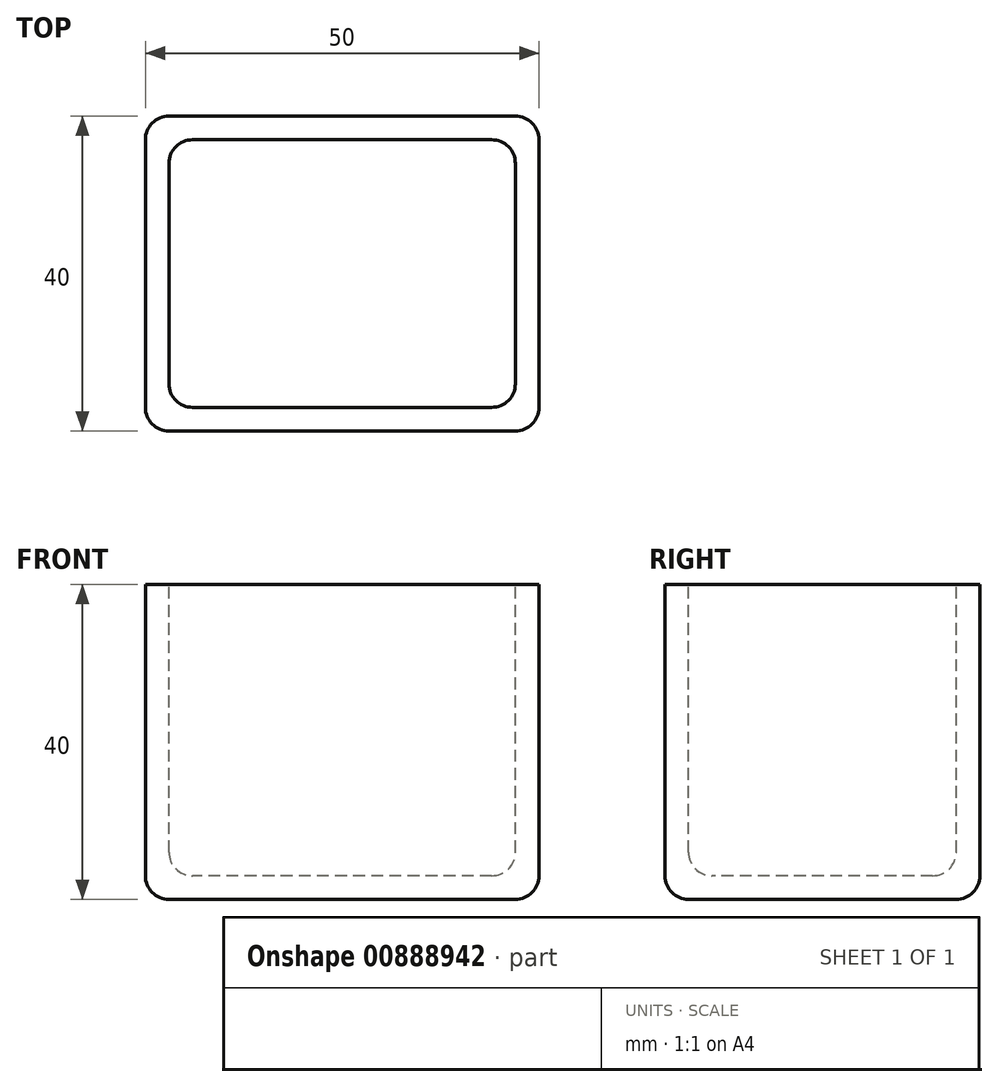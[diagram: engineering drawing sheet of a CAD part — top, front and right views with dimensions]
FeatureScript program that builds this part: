
annotation { "Feature Type Name" : "Feature", "Feature Type Description" : "" }
export const myFeature = defineFeature(function(context is Context, id is Id, definition is map)
    precondition{}
    {
        {
            var Q0;
            Q0=qCreatedBy(makeId("Top.planeOp"),FACE);
            var sketch = newSketch(context, id + "F0", { "sketchPlane" : qUnion([Q0])});
            skLineSegment(sketch, "E0.bottom", {"start": v(-25, 40) * mm, "end": v(25, 40) * mm});
            skLineSegment(sketch, "E0.top", {"start": v(-25, 0) * mm, "end": v(25, 0) * mm});
            skLineSegment(sketch, "E0.left", {"start": v(-25, 40) * mm, "end": v(-25, 0) * mm});
            skLineSegment(sketch, "E0.right", {"start": v(25, 40) * mm, "end": v(25, 0) * mm});
            skSolve(sketch);
        }
        {
            var Q0;
            Q0=makeQuery(id+"F0.imprint","IMPRINT",FACE,{"disambiguationData":[TD([[makeQuery(id+"F0.imprint","IMPRINT",EDGE,{"derivedFrom":sQuery(id+"F0.wireOp",EDGE,"E0.bottom")}),-1.0]])]});
            extrude(context, id + "F1", {"entities" : qUnion([Q0]), "depth" : 40 * mm, "offsetDistance" : 25 * mm});
        }
        {
            var Q0;
            Q0=makeQuery(id+"F1.opExtrude","CAP_FACE",FACE,{"disambiguationData":[OSD([sQuery(id+"F0.wireOp",EDGE,"E0.bottom"),sQuery(id+"F0.wireOp",EDGE,"E0.top"),sQuery(id+"F0.wireOp",EDGE,"E0.left"),sQuery(id+"F0.wireOp",EDGE,"E0.right")])],"isStart":false});
            var sketch = newSketch(context, id + "F2", { "sketchPlane" : qUnion([Q0])});
            skLineSegment(sketch, "E1.bottom", {"start": v(22, 37) * mm, "end": v(-22, 37) * mm});
            skLineSegment(sketch, "E1.top", {"start": v(22, 3) * mm, "end": v(-22, 3) * mm});
            skLineSegment(sketch, "E1.left", {"start": v(22, 37) * mm, "end": v(22, 3) * mm});
            skLineSegment(sketch, "E1.right", {"start": v(-22, 37) * mm, "end": v(-22, 3) * mm});
            skPoint(sketch, "E1.middle", {"position": v(0, 20) * mm});
            skSolve(sketch);
        }
        {
            var Q0;
            Q0 = qSketchRegion(id + "F2", true);
            extrude(context, id + "F3", {"entities" : qUnion([Q0]), "operationType" : NewBodyOperationType.REMOVE, "oppositeDirection" : true, "depth" : 37 * mm, "offsetDistance" : 25 * mm});
        }
        {
            var Q0;
            Q0=makeQuery(id+"F3.boolean.opBoolean","COPY",EDGE,{"derivedFrom":makeQuery(id+"F3.opExtrude","SWEPT_EDGE",EDGE,{"disambiguationData":[OSD([sQuery(id+"F2.wireOp",EDGE,"E1.bottom"),sQuery(id+"F2.wireOp",EDGE,"E1.right")])]})});
            var Q1;
            Q1=makeQuery(id+"F3.boolean.opBoolean","COPY",EDGE,{"derivedFrom":makeQuery(id+"F3.opExtrude","CAP_EDGE",EDGE,{"disambiguationData":[OSD([sQuery(id+"F2.wireOp",EDGE,"E1.bottom")])],"isStart":false})});
            var Q2;
            Q2=makeQuery(id+"F3.boolean.opBoolean","COPY",EDGE,{"derivedFrom":makeQuery(id+"F3.opExtrude","CAP_EDGE",EDGE,{"disambiguationData":[OSD([sQuery(id+"F2.wireOp",EDGE,"E1.right")])],"isStart":false})});
            var Q3;
            Q3=makeQuery(id+"F3.boolean.opBoolean","COPY",EDGE,{"derivedFrom":makeQuery(id+"F3.opExtrude","SWEPT_EDGE",EDGE,{"disambiguationData":[OSD([sQuery(id+"F2.wireOp",EDGE,"E1.top"),sQuery(id+"F2.wireOp",EDGE,"E1.right")])]})});
            var Q4;
            Q4=makeQuery(id+"F3.boolean.opBoolean","COPY",EDGE,{"derivedFrom":makeQuery(id+"F3.opExtrude","CAP_EDGE",EDGE,{"disambiguationData":[OSD([sQuery(id+"F2.wireOp",EDGE,"E1.top")])],"isStart":false})});
            var Q5;
            Q5=makeQuery(id+"F3.boolean.opBoolean","COPY",EDGE,{"derivedFrom":makeQuery(id+"F3.opExtrude","CAP_EDGE",EDGE,{"disambiguationData":[OSD([sQuery(id+"F2.wireOp",EDGE,"E1.left")])],"isStart":false})});
            var Q6;
            Q6=makeQuery(id+"F3.boolean.opBoolean","COPY",EDGE,{"derivedFrom":makeQuery(id+"F3.opExtrude","SWEPT_EDGE",EDGE,{"disambiguationData":[OSD([sQuery(id+"F2.wireOp",EDGE,"E1.bottom"),sQuery(id+"F2.wireOp",EDGE,"E1.left")])]})});
            var Q7;
            Q7=makeQuery(id+"F3.boolean.opBoolean","COPY",EDGE,{"derivedFrom":makeQuery(id+"F3.opExtrude","SWEPT_EDGE",EDGE,{"disambiguationData":[OSD([sQuery(id+"F2.wireOp",EDGE,"E1.top"),sQuery(id+"F2.wireOp",EDGE,"E1.left")])]})});
            fillet(context, id + "F4", {"entities" : qUnion([Q0, Q1, Q2, Q3, Q4, Q5, Q6, Q7]), "radius" : 3 * mm, "tangentPropagation" : true, "allowEdgeOverflow" : false});
        }
        {
            var Q0;
            Q0=makeQuery(id+"F1.opExtrude","SWEPT_EDGE",EDGE,{"disambiguationData":[OSD([sQuery(id+"F0.wireOp",EDGE,"E0.top"),sQuery(id+"F0.wireOp",EDGE,"E0.left")])]});
            var Q1;
            Q1=makeQuery(id+"F1.opExtrude","SWEPT_EDGE",EDGE,{"disambiguationData":[OSD([sQuery(id+"F0.wireOp",EDGE,"E0.top"),sQuery(id+"F0.wireOp",EDGE,"E0.right")])]});
            var Q2;
            Q2=makeQuery(id+"F1.opExtrude","CAP_EDGE",EDGE,{"disambiguationData":[OSD([sQuery(id+"F0.wireOp",EDGE,"E0.top")])],"isStart":true});
            var Q3;
            Q3=makeQuery(id+"F1.opExtrude","CAP_EDGE",EDGE,{"disambiguationData":[OSD([sQuery(id+"F0.wireOp",EDGE,"E0.left")])],"isStart":true});
            var Q4;
            Q4=makeQuery(id+"F1.opExtrude","SWEPT_EDGE",EDGE,{"disambiguationData":[OSD([sQuery(id+"F0.wireOp",EDGE,"E0.bottom"),sQuery(id+"F0.wireOp",EDGE,"E0.left")])]});
            var Q5;
            Q5=makeQuery(id+"F1.opExtrude","CAP_EDGE",EDGE,{"disambiguationData":[OSD([sQuery(id+"F0.wireOp",EDGE,"E0.bottom")])],"isStart":true});
            var Q6;
            Q6=makeQuery(id+"F1.opExtrude","CAP_EDGE",EDGE,{"disambiguationData":[OSD([sQuery(id+"F0.wireOp",EDGE,"E0.right")])],"isStart":true});
            var Q7;
            Q7=makeQuery(id+"F1.opExtrude","SWEPT_EDGE",EDGE,{"disambiguationData":[OSD([sQuery(id+"F0.wireOp",EDGE,"E0.bottom"),sQuery(id+"F0.wireOp",EDGE,"E0.right")])]});
            fillet(context, id + "F5", {"entities" : qUnion([Q0, Q1, Q2, Q3, Q4, Q5, Q6, Q7]), "radius" : 3 * mm, "tangentPropagation" : true, "allowEdgeOverflow" : false});
        }
    });
